# Revit family: Haworth_Pergola_Accessory_CoatHook_PRELIM
name_source: partatom
category: Furniture Systems
revit_build: Autodesk Revit 2018 (Build: 20170223_1515(x64)
units: mm (PartAtom-declared; Revit-internal decimal feet)

## family parameters
Always vertical = Yes
Cut with Voids When Loaded = No
OmniClass Number = 23.40.20.00
OmniClass Title = General Furniture and Specialties
Part Type = Normal
Room Calculation Point = No
Round Connector Dimension = Use Diameter
Shared = No
Work Plane-Based = No

## types (1)
- Coat Hook
    Assembly Code = E2020200
    Description = Haworth - Pergola - Accessories - Coat Hook
    Manufacturer = Haworth
    Size = Verify Final Dim. w/ Haworth
    Standard Length = 4.5, 31.25, and 55.25 in.
    Sustainability Info = https://www.haworth.com
    URL = http://haworthcollection.com
    URL Product = https://www.haworth.com
    Version = 1
    Warranty = http://www.haworth.com

## geometry (parser evidence)
native form markers: Sweep x5
no freeform markers — native parametric forms only
